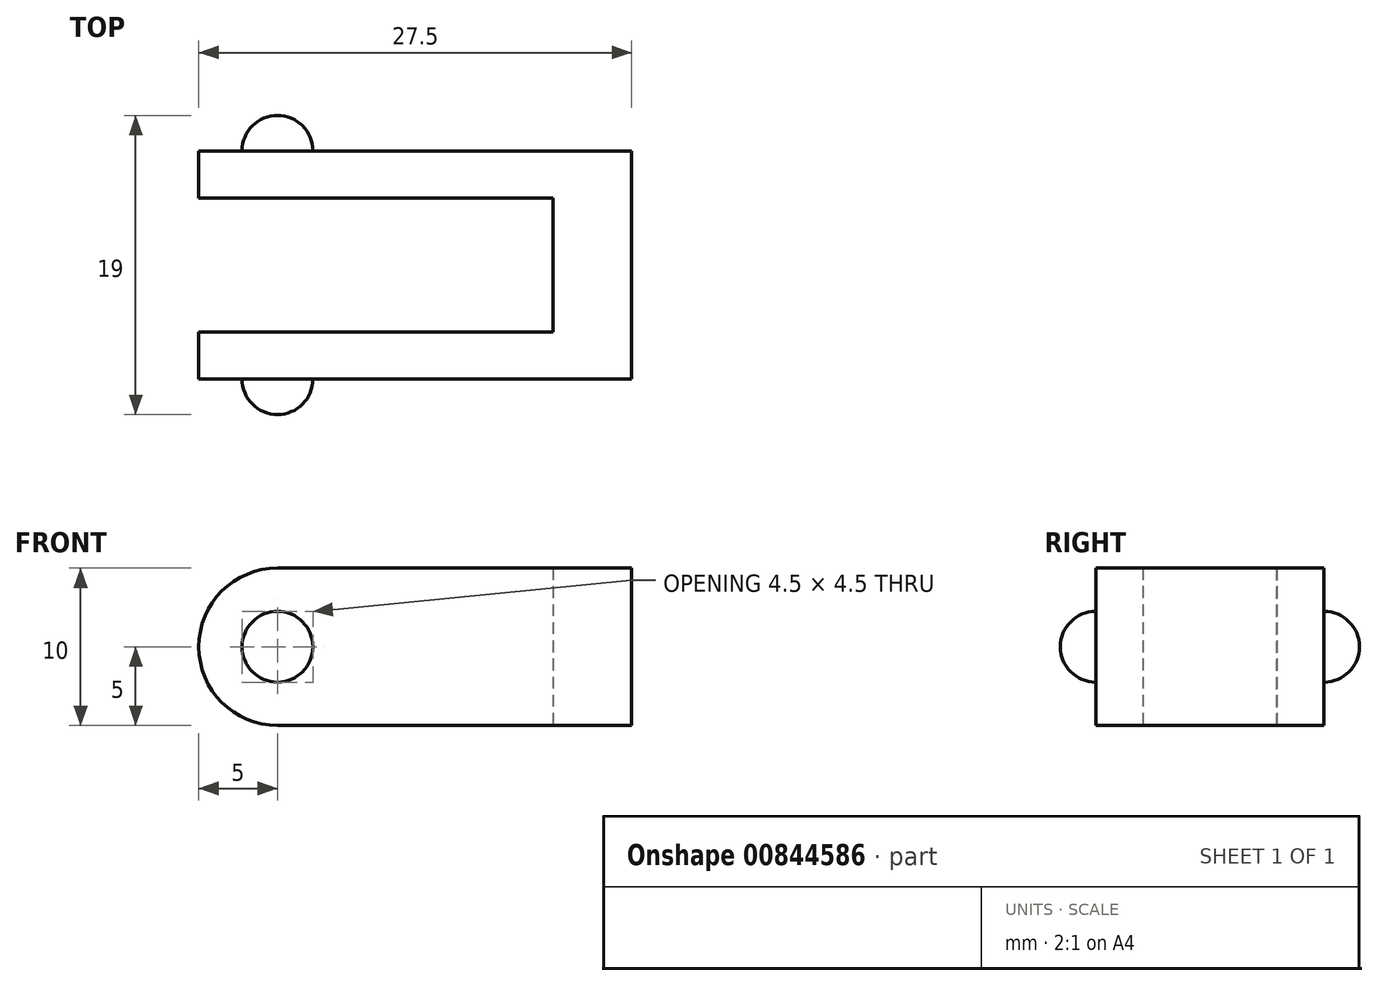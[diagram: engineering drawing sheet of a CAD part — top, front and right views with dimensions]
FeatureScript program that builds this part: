
annotation { "Feature Type Name" : "Feature", "Feature Type Description" : "" }
export const myFeature = defineFeature(function(context is Context, id is Id, definition is map)
    precondition{}
    {
        {
            var Q0;
            Q0=qCreatedBy(makeId("Top.planeOp"),FACE);
            var sketch = newSketch(context, id + "F0", { "sketchPlane" : qUnion([Q0])});
            skLineSegment(sketch, "E0.bottom", {"start": v(25, 0) * mm, "end": v(30, 0) * mm});
            skLineSegment(sketch, "E0.top", {"start": v(0, 7.25) * mm, "end": v(30, 7.25) * mm});
            skLineSegment(sketch, "E0.left", {"start": v(0, 4.25) * mm, "end": v(0, 7.25) * mm});
            skLineSegment(sketch, "E0.right", {"start": v(30, 0) * mm, "end": v(30, 7.25) * mm});
            skLineSegment(sketch, "E1.top", {"start": v(0, 4.25) * mm, "end": v(25, 4.25) * mm});
            skLineSegment(sketch, "E1.right", {"start": v(25, 0) * mm, "end": v(25, 4.25) * mm});
            skSolve(sketch);
        }
        {
            var Q0;
            Q0=makeQuery(id+"F0.imprint","IMPRINT",FACE,{"disambiguationData":[TD([[makeQuery(id+"F0.imprint","IMPRINT",EDGE,{"derivedFrom":sQuery(id+"F0.wireOp",EDGE,"E0.bottom")}),1.0]])]});
            extrude(context, id + "F1", {"entities" : qUnion([Q0]), "depth" : 10 * mm, "offsetDistance" : 25 * mm});
        }
        {
            var Q0;
            Q0=makeQuery(id+"F1.opExtrude","SWEPT_FACE",FACE,{"disambiguationData":[OSD([sQuery(id+"F0.wireOp",EDGE,"E0.top")])]});
            var sketch = newSketch(context, id + "F2", { "sketchPlane" : qUnion([Q0])});
            skArc(sketch, "E2", {"start": v(-7.5, 2.75) * mm, "mid": v(-5.25, 5) * mm, "end": v(-7.5, 7.25) * mm});
            skPoint(sketch, "E3", {"position": v(-7.5, 10) * mm});
            skLineSegment(sketch, "E4", {"start": v(-7.5, 7.25) * mm, "end": v(-7.5, 2.75) * mm});
            skSolve(sketch);
        }
        {
            var Q0;
            Q0 = qSketchRegion(id + "F2", true);
            var Q1;
            Q1=sQuery(id+"F2.wireOp",EDGE,"E4");
            revolve(context, id + "F3", {"operationType" : NewBodyOperationType.ADD, "surfaceOperationType" : NewSurfaceOperationType.NEW, "entities" : qUnion([Q0]), "axis" : qUnion([Q1]), "revolveType" : RevolveType.FULL});
        }
        {
            var Q0;
            Q0=makeQuery(id+"F1.opExtrude","SWEPT_BODY",BODY,{"disambiguationData":[OSD([sQuery(id+"F0.wireOp",EDGE,"E0.bottom"),sQuery(id+"F0.wireOp",EDGE,"E0.top"),sQuery(id+"F0.wireOp",EDGE,"E0.left"),sQuery(id+"F0.wireOp",EDGE,"E0.right")])]});
            var Q1;
            Q1=qCreatedBy(makeId("Front.planeOp"),FACE);
            mirror(context, id + "F4", {"operationType" : NewBodyOperationType.ADD, "entities" : qUnion([Q0]), "mirrorPlane" : qUnion([Q1])});
        }
        {
            var Q0;
            Q0=makeQuery(id+"F4.opPattern","COPY",FACE,{"derivedFrom":makeQuery(id+"F1.opExtrude","SWEPT_FACE",FACE,{"disambiguationData":[OSD([sQuery(id+"F0.wireOp",EDGE,"E0.top")])]}),"instanceName":"1"});
            var sketch = newSketch(context, id + "F5", { "sketchPlane" : qUnion([Q0])});
            skArc(sketch, "E5", {"start": v(7.5, 10) * mm, "mid": v(2.5, 5) * mm, "end": v(7.5, 0) * mm});
            skSolve(sketch);
        }
        {
            var Q0;
            {var subQ0=sQuery(id+"F5.wireOp",EDGE,"E5");var subQ1=sQuery(id+"F0.wireOp",EDGE,"E0.top");var subQ2=makeQuery(id+"F4.opPattern","COPY",EDGE,{"derivedFrom":makeQuery(id+"F1.opExtrude","CAP_EDGE",EDGE,{"disambiguationData":[OSD([subQ1])],"isStart":false}),"instanceName":"1"});var subQ3=makeQuery(id+"F5.imprint","INTERSECT",VERTEX,{"derivedFrom":[subQ2,subQ0]});Q0=makeQuery(id+"F5.imprint","IMPRINT",FACE,{"disambiguationData":[TD([[makeQuery(id+"F5.imprint","IMPRINT",EDGE,{"disambiguationData":[TD([[subQ3,-1.0]])],"derivedFrom":subQ0}),-1.0]])]});}
            var Q1;
            {var subQ0=sQuery(id+"F5.wireOp",EDGE,"E5");var subQ1=sQuery(id+"F0.wireOp",EDGE,"E0.top");var subQ2=makeQuery(id+"F4.opPattern","COPY",EDGE,{"derivedFrom":makeQuery(id+"F1.opExtrude","CAP_EDGE",EDGE,{"disambiguationData":[OSD([subQ1])],"isStart":true}),"instanceName":"1"});var subQ3=makeQuery(id+"F5.imprint","INTERSECT",VERTEX,{"derivedFrom":[subQ2,subQ0]});Q1=makeQuery(id+"F5.imprint","IMPRINT",FACE,{"disambiguationData":[TD([[makeQuery(id+"F5.imprint","IMPRINT",EDGE,{"disambiguationData":[TD([[subQ3,1.0]])],"derivedFrom":subQ0}),-1.0]])]});}
            extrude(context, id + "F6", {"entities" : qUnion([Q0, Q1]), "operationType" : NewBodyOperationType.REMOVE, "oppositeDirection" : true, "depth" : 25 * mm, "offsetDistance" : 25 * mm});
        }
    });
